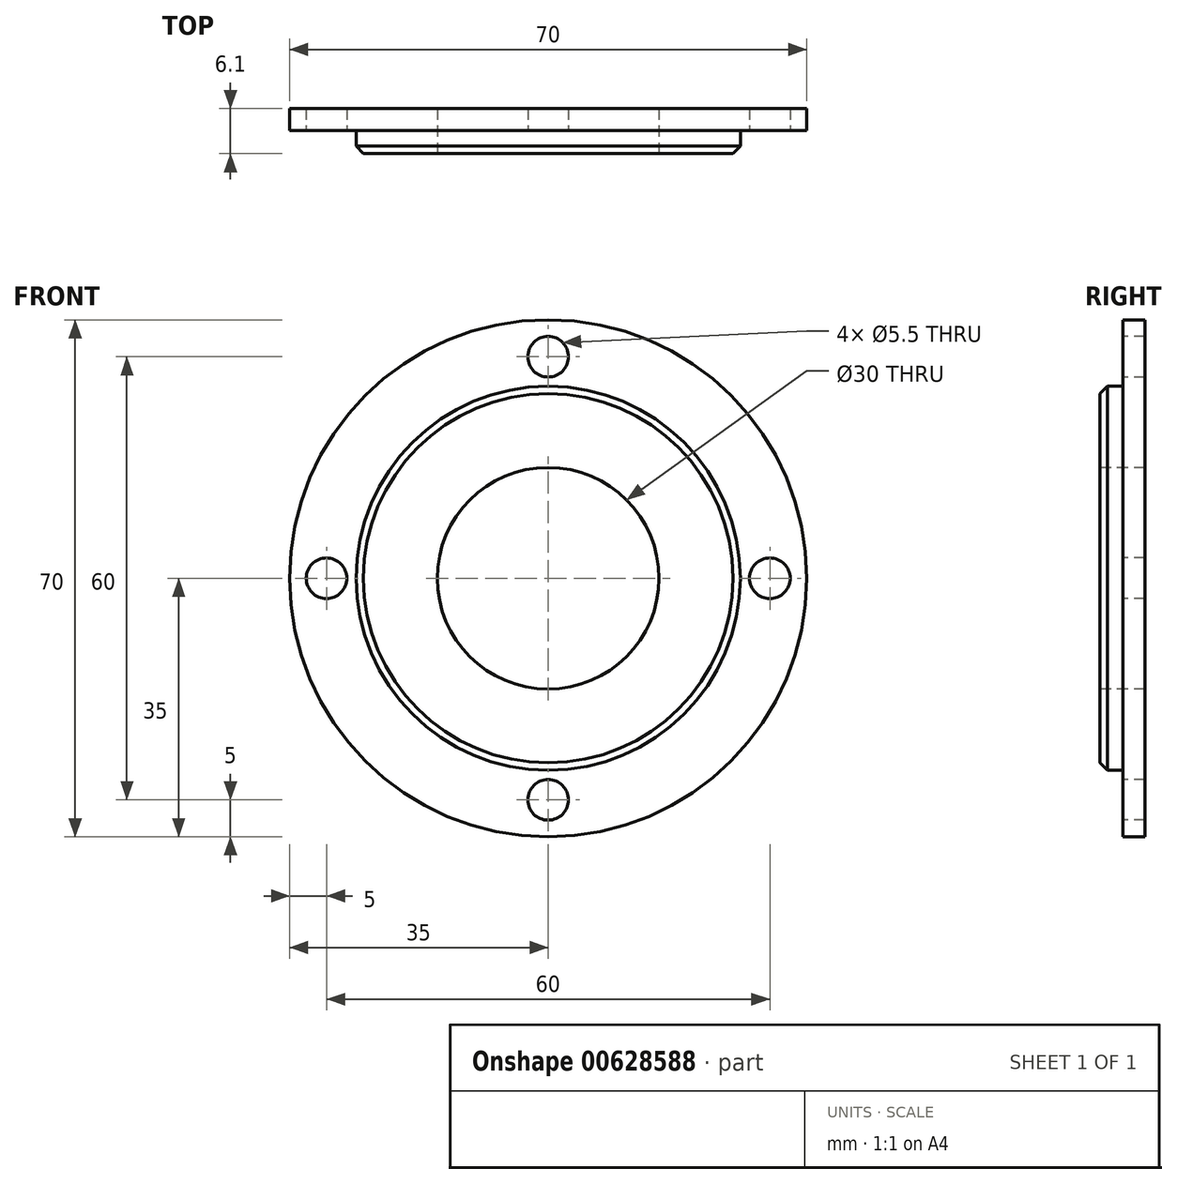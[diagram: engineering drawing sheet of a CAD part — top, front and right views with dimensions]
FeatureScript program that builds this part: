
annotation { "Feature Type Name" : "Feature", "Feature Type Description" : "" }
export const myFeature = defineFeature(function(context is Context, id is Id, definition is map)
    precondition{}
    {
        {
            var Q0;
            Q0=qCreatedBy(makeId("Front.planeOp"),FACE);
            var sketch = newSketch(context, id + "F0", { "sketchPlane" : qUnion([Q0])});
            skCircle(sketch, "E0", {"center": v(0, 0) * mm, "radius": 35 * mm});
            skSolve(sketch);
        }
        {
            var Q0;
            Q0 = qSketchRegion(id + "F0", true);
            extrude(context, id + "F1", {"entities" : qUnion([Q0]), "depth" : 3 * mm, "offsetDistance" : 25 * mm});
        }
        {
            var Q0;
            Q0=makeQuery(id+"F1.opExtrude","CAP_FACE",FACE,{"disambiguationData":[OSD([sQuery(id+"F0.wireOp",EDGE,"E0")])],"isStart":false});
            var sketch = newSketch(context, id + "F2", { "sketchPlane" : qUnion([Q0])});
            skCircle(sketch, "E1", {"center": v(0, 0) * mm, "radius": 30 * mm, "construction": true});
            skLineSegment(sketch, "E2", {"start": v(0, 0) * mm, "end": v(42.47, 0) * mm, "construction": true});
            skLineSegment(sketch, "E3", {"start": v(0, 0) * mm, "end": v(0, 44.53) * mm, "construction": true});
            skCircle(sketch, "E4", {"center": v(30, 0) * mm, "radius": 2.75 * mm});
            skCircle(sketch, "E5", {"center": v(0, 30) * mm, "radius": 2.75 * mm});
            skCircle(sketch, "E6.MirrorC", {"center": v(-30, 0) * mm, "radius": 2.75 * mm});
            skCircle(sketch, "E7.MirrorC", {"center": v(0, -30) * mm, "radius": 2.75 * mm});
            skSolve(sketch);
        }
        {
            var Q0;
            Q0 = qSketchRegion(id + "F2", true);
            extrude(context, id + "F3", {"entities" : qUnion([Q0]), "operationType" : NewBodyOperationType.REMOVE, "endBound" : BoundingType.UP_TO_NEXT, "oppositeDirection" : true, "depth" : 25 * mm, "offsetDistance" : 25 * mm});
        }
        {
            var Q0;
            Q0=makeQuery(id+"F1.opExtrude","CAP_FACE",FACE,{"disambiguationData":[OSD([sQuery(id+"F0.wireOp",EDGE,"E0")])],"isStart":false});
            var sketch = newSketch(context, id + "F4", { "sketchPlane" : qUnion([Q0])});
            skCircle(sketch, "E8", {"center": v(0, 0) * mm, "radius": 26 * mm});
            skSolve(sketch);
        }
        {
            var Q0;
            Q0 = qSketchRegion(id + "F4", true);
            extrude(context, id + "F5", {"entities" : qUnion([Q0]), "operationType" : NewBodyOperationType.ADD, "depth" : 3.1 * mm, "offsetDistance" : 25 * mm});
        }
        {
            var Q0;
            Q0=makeQuery(id+"F5.opExtrude","CAP_FACE",FACE,{"disambiguationData":[OSD([sQuery(id+"F4.wireOp",EDGE,"E8")])],"isStart":false});
            var sketch = newSketch(context, id + "F6", { "sketchPlane" : qUnion([Q0])});
            skCircle(sketch, "E9", {"center": v(0, 0) * mm, "radius": 15 * mm});
            skSolve(sketch);
        }
        {
            var Q0;
            Q0 = qSketchRegion(id + "F6", true);
            extrude(context, id + "F7", {"entities" : qUnion([Q0]), "operationType" : NewBodyOperationType.REMOVE, "endBound" : BoundingType.UP_TO_NEXT, "oppositeDirection" : true, "depth" : 25 * mm, "offsetDistance" : 25 * mm});
        }
        {
            var Q0;
            Q0=makeQuery(id+"F5.opExtrude","CAP_EDGE",EDGE,{"disambiguationData":[OSD([sQuery(id+"F4.wireOp",EDGE,"E8")])],"isStart":false});
            chamfer(context, id + "F8", {"entities" : qUnion([Q0]), "width" : 1 * mm, "tangentPropagation" : true});
        }
    });
